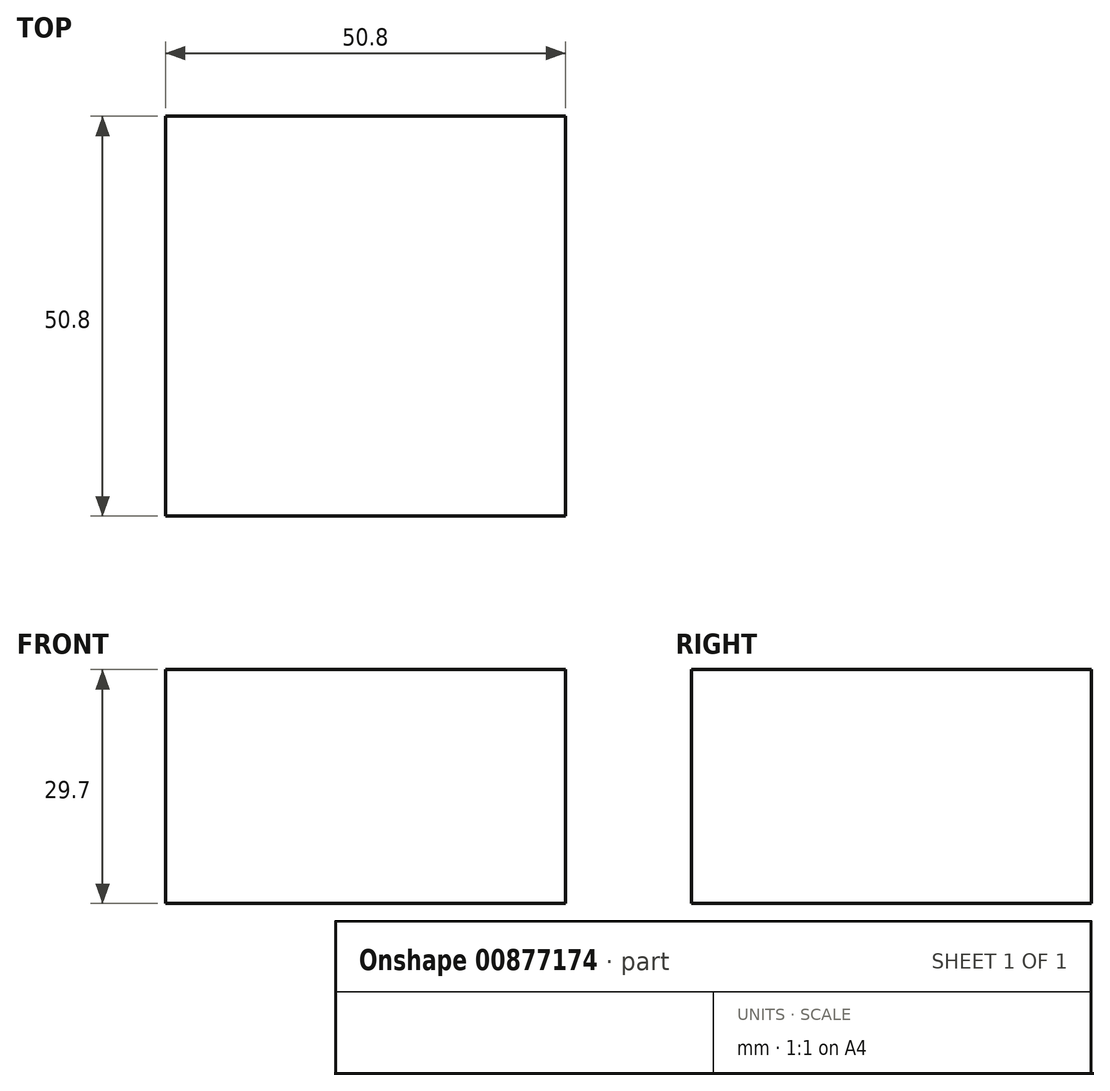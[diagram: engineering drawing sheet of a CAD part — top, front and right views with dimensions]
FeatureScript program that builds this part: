
annotation { "Feature Type Name" : "Feature", "Feature Type Description" : "" }
export const myFeature = defineFeature(function(context is Context, id is Id, definition is map)
    precondition{}
    {
        {
            var Q0;
            Q0=qCreatedBy(makeId("Top.planeOp"),FACE);
            var sketch = newSketch(context, id + "F0", { "sketchPlane" : qUnion([Q0])});
            skLineSegment(sketch, "E0.bottom", {"start": v(25.4, 25.4) * mm, "end": v(-25.4, 25.4) * mm});
            skLineSegment(sketch, "E0.top", {"start": v(25.4, -25.4) * mm, "end": v(-25.4, -25.4) * mm});
            skLineSegment(sketch, "E0.left", {"start": v(25.4, 25.4) * mm, "end": v(25.4, -25.4) * mm});
            skLineSegment(sketch, "E0.right", {"start": v(-25.4, 25.4) * mm, "end": v(-25.4, -25.4) * mm});
            skPoint(sketch, "E0.middle", {"position": v(0, 0) * mm});
            skSolve(sketch);
        }
        {
            var Q0;
            Q0 = qSketchRegion(id + "F0", true);
            extrude(context, id + "F1", {"entities" : qUnion([Q0]), "depth" : 29.7 * mm, "offsetDistance" : 25 * mm});
        }
    });
